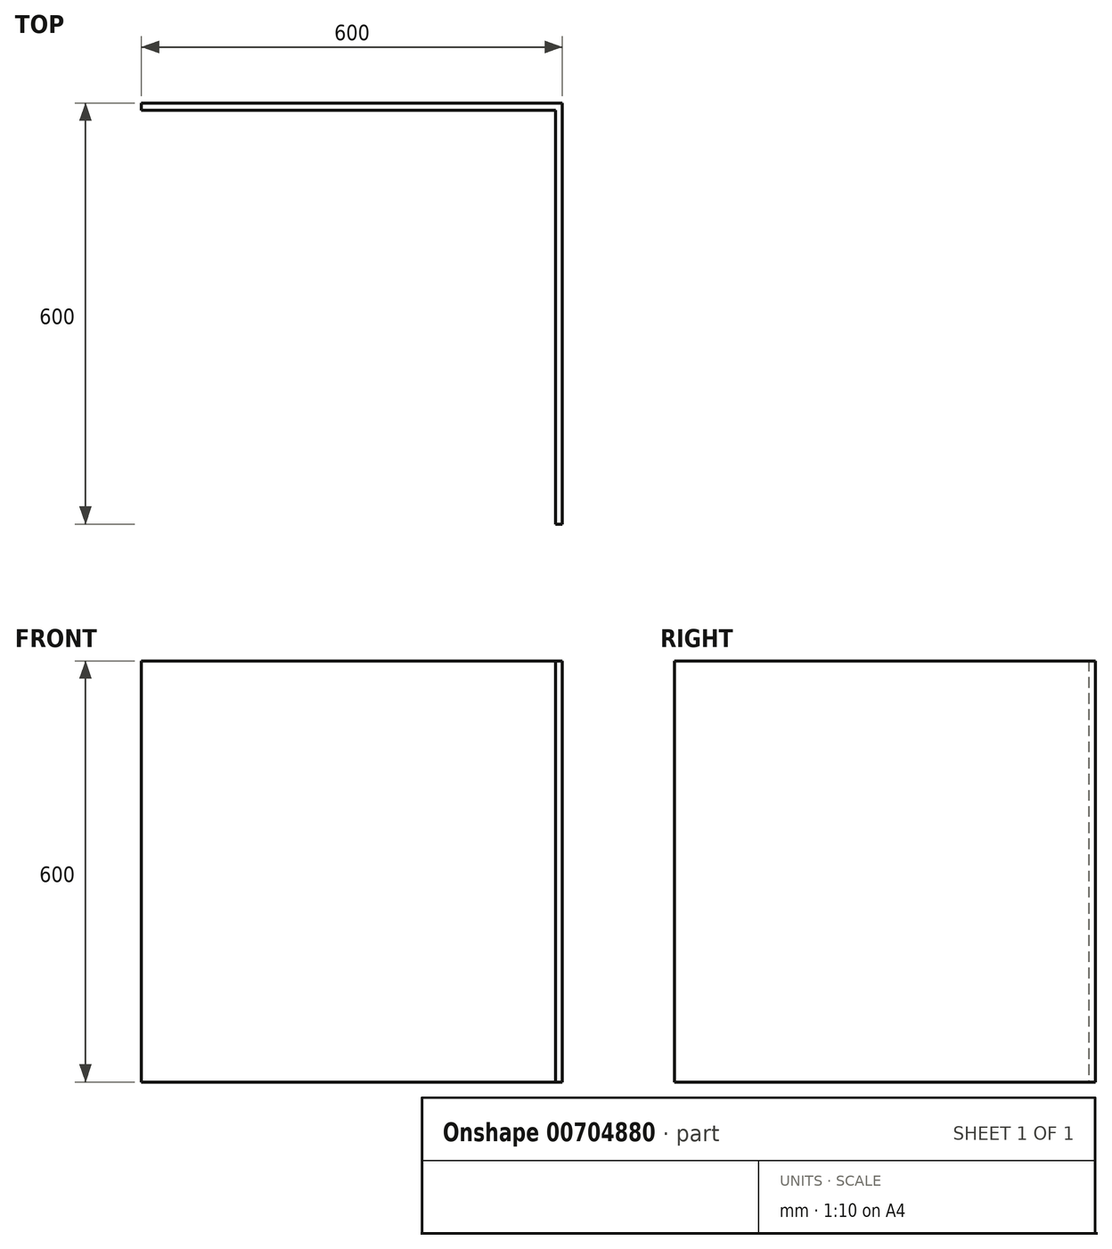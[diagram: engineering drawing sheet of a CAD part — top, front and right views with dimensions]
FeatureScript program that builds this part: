
annotation { "Feature Type Name" : "Feature", "Feature Type Description" : "" }
export const myFeature = defineFeature(function(context is Context, id is Id, definition is map)
    precondition{}
    {
        {
            var Q0;
            Q0=qCreatedBy(makeId("Top.planeOp"),FACE);
            var sketch = newSketch(context, id + "F0", { "sketchPlane" : qUnion([Q0])});
            skLineSegment(sketch, "E0", {"start": v(0, 0) * mm, "end": v(-600, 0) * mm});
            skLineSegment(sketch, "E1", {"start": v(0, 0) * mm, "end": v(0, -600) * mm});
            skLineSegment(sketch, "E2", {"start": v(-600, 0) * mm, "end": v(-600, -10) * mm});
            skLineSegment(sketch, "E3", {"start": v(-600, -10) * mm, "end": v(-10, -10) * mm});
            skLineSegment(sketch, "E4", {"start": v(0, -600) * mm, "end": v(-10, -600) * mm});
            skLineSegment(sketch, "E5", {"start": v(-10, -600) * mm, "end": v(-10, -10) * mm});
            skPoint(sketch, "E6.orphan", {"position": v(0, -10) * mm});
            skSolve(sketch);
        }
        {
            var Q0;
            Q0 = qSketchRegion(id + "F0", true);
            extrude(context, id + "F1", {"entities" : qUnion([Q0]), "depth" : 600 * mm, "offsetDistance" : 25.4 * mm});
        }
    });
